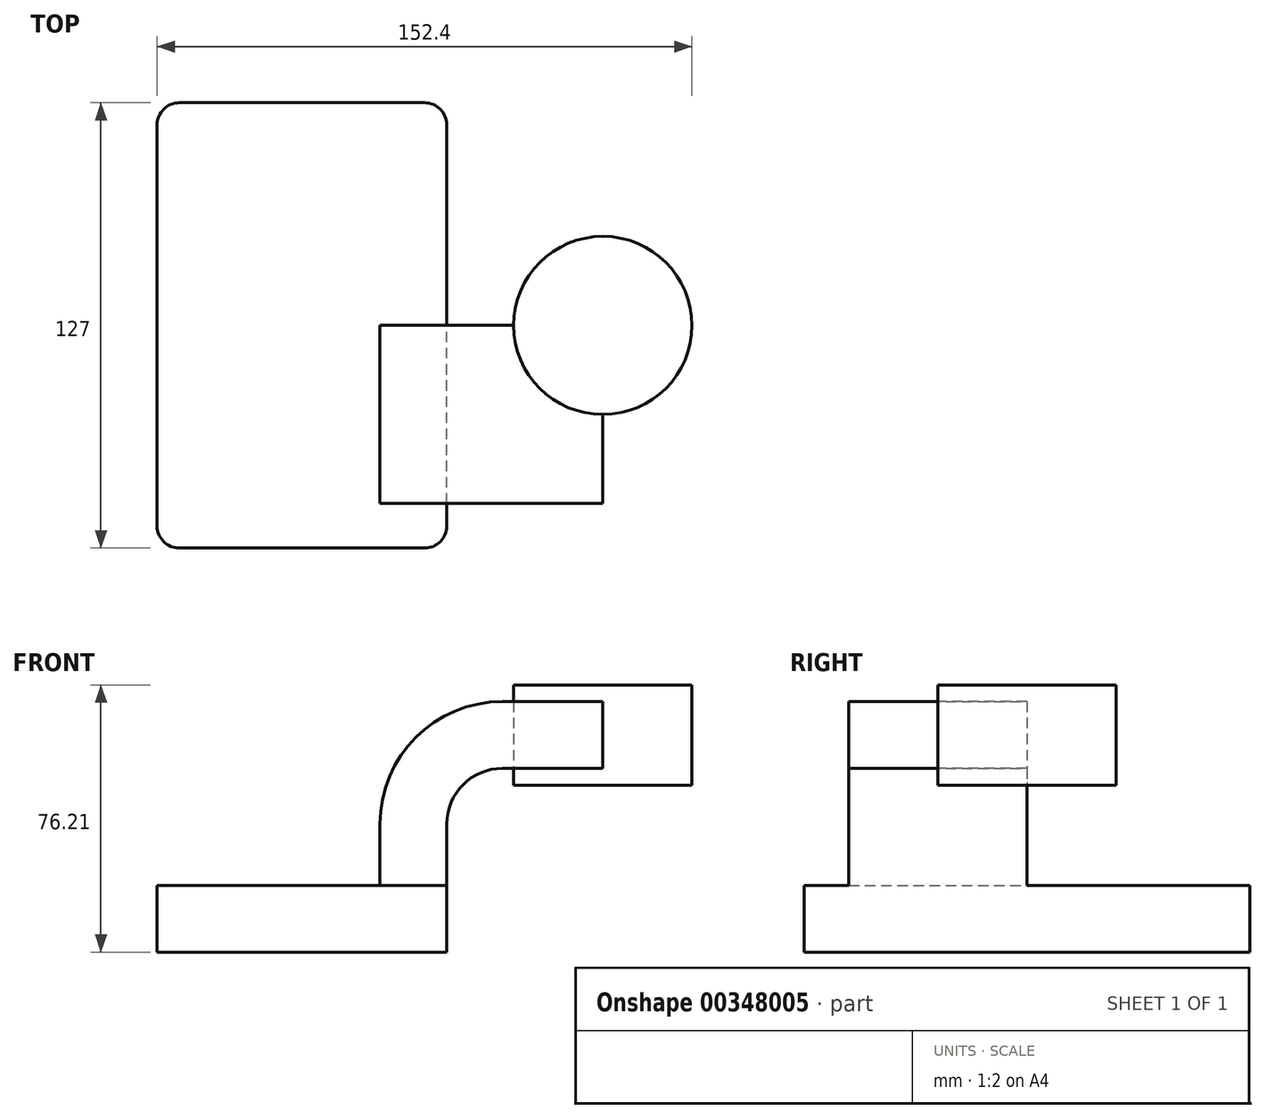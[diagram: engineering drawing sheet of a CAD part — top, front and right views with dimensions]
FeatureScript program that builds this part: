
annotation { "Feature Type Name" : "Feature", "Feature Type Description" : "" }
export const myFeature = defineFeature(function(context is Context, id is Id, definition is map)
    precondition{}
    {
        {
            var Q0;
            Q0=qCreatedBy(makeId("Front.planeOp"),FACE);
            var sketch = newSketch(context, id + "F0", { "sketchPlane" : qUnion([Q0])});
            skLineSegment(sketch, "E0.bottom", {"start": v(41.27, 9.53) * mm, "end": v(-41.28, 9.53) * mm});
            skLineSegment(sketch, "E0.top", {"start": v(41.28, -9.52) * mm, "end": v(-41.27, -9.52) * mm});
            skLineSegment(sketch, "E0.left", {"start": v(41.28, 9.53) * mm, "end": v(41.28, -9.52) * mm});
            skLineSegment(sketch, "E0.right", {"start": v(-41.28, 9.53) * mm, "end": v(-41.27, -9.52) * mm});
            skPoint(sketch, "E0.middle", {"position": v(0, 0) * mm});
            skLineSegment(sketch, "E1.bottom", {"start": v(111.12, 38.1) * mm, "end": v(60.32, 38.1) * mm});
            skLineSegment(sketch, "E1.top", {"start": v(111.12, 66.68) * mm, "end": v(60.32, 66.68) * mm});
            skLineSegment(sketch, "E1.left", {"start": v(111.12, 38.1) * mm, "end": v(111.12, 66.68) * mm});
            skLineSegment(sketch, "E1.right", {"start": v(60.32, 38.1) * mm, "end": v(60.32, 66.68) * mm});
            skPoint(sketch, "E1.middle", {"position": v(85.73, 52.39) * mm});
            skLineSegment(sketch, "E2", {"start": v(41.27, 9.53) * mm, "end": v(41.27, 27) * mm});
            skArc(sketch, "E3", {"start": v(41.28, 27) * mm, "mid": v(45.92, 38.23) * mm, "end": v(57.15, 42.88) * mm});
            skLineSegment(sketch, "E4", {"start": v(57.15, 42.88) * mm, "end": v(74.94, 42.88) * mm});
            skLineSegment(sketch, "E5", {"start": v(74.94, 42.88) * mm, "end": v(86.6, 42.88) * mm});
            skLineSegment(sketch, "E6", {"start": v(109.19, -23.17) * mm, "end": v(107.34, -21.62) * mm});
            skLineSegment(sketch, "E7.0", {"start": v(74.94, 61.93) * mm, "end": v(85.73, 61.93) * mm});
            skLineSegment(sketch, "E7.1", {"start": v(57.15, 61.93) * mm, "end": v(74.94, 61.93) * mm});
            skArc(sketch, "E7.2", {"start": v(22.23, 27) * mm, "mid": v(32.45, 51.7) * mm, "end": v(57.15, 61.93) * mm});
            skLineSegment(sketch, "E7.3", {"start": v(22.22, 9.53) * mm, "end": v(22.22, 27) * mm});
            skLineSegment(sketch, "E8", {"start": v(85.73, 38.1) * mm, "end": v(85.73, 66.68) * mm});
            skFitSpline(sketch, "E9", {"points": [v(-41.28, 9.53) * mm, v(57.15, 61.93) * mm], "startDerivative": vector(0.12, 127.1) * mm, "endDerivative": vector(139.48, -7.9) * mm});
            skSolve(sketch);
        }
        {
            var Q0;
            Q0=makeQuery(id+"F0.imprint","IMPRINT",FACE,{"disambiguationData":[TD([[makeQuery(id+"F0.imprint","IMPRINT",EDGE,{"derivedFrom":sQuery(id+"F0.wireOp",EDGE,"E0.top")}),-1.0]])]});
            extrude(context, id + "F1", {"entities" : qUnion([Q0]), "endBound" : BoundingType.SYMMETRIC, "depth" : 127 * mm});
        }
        {
            var Q0;
            {var subQ1=sQuery(id+"F0.wireOp",EDGE,"E2");Q0=makeQuery(id+"F0.imprint","IMPRINT",FACE,{"disambiguationData":[TD([[makeQuery(id+"F0.imprint","IMPRINT",EDGE,{"derivedFrom":subQ1}),1.0]])]});}
            var Q1;
            {var subQ0=sQuery(id+"F0.wireOp",EDGE,"E7.0");Q1=makeQuery(id+"F0.imprint","IMPRINT",FACE,{"disambiguationData":[TD([[makeQuery(id+"F0.imprint","IMPRINT",EDGE,{"derivedFrom":subQ0}),-1.0]])]});}
            extrude(context, id + "F2", {"entities" : qUnion([Q0, Q1]), "operationType" : NewBodyOperationType.ADD, "depth" : 50.8 * mm});
        }
        {
            var Q0;
            Q0=makeQuery(id+"F0.imprint","IMPRINT",FACE,{"disambiguationData":[TD([[makeQuery(id+"F0.imprint","IMPRINT",EDGE,{"derivedFrom":sQuery(id+"F0.wireOp",EDGE,"E7.2")}),1.0]])]});
            extrude(context, id + "F3", {"entities" : qUnion([Q0]), "operationType" : NewBodyOperationType.ADD, "depth" : 15.88 * mm});
        }
        {
            var Q0;
            {var subQ4=sQuery(id+"F0.wireOp",EDGE,"E1.left");Q0=makeQuery(id+"F0.imprint","IMPRINT",FACE,{"disambiguationData":[TD([[makeQuery(id+"F0.imprint","IMPRINT",EDGE,{"derivedFrom":subQ4}),1.0]])]});}
            var Q1;
            Q1=sQuery(id+"F0.wireOp",EDGE,"E8");
            revolve(context, id + "F4", {"operationType" : NewBodyOperationType.ADD, "entities" : qUnion([Q0]), "axis" : qUnion([Q1]), "revolveType" : RevolveType.FULL});
        }
        {
            var Q0;
            Q0=makeQuery(id+"F1.opExtrude","CAP_EDGE",EDGE,{"disambiguationData":[OSD([sQuery(id+"F0.wireOp",EDGE,"E0.right")])],"isStart":false});
            var Q1;
            Q1=makeQuery(id+"F1.opExtrude","CAP_EDGE",EDGE,{"disambiguationData":[OSD([sQuery(id+"F0.wireOp",EDGE,"E0.left")])],"isStart":false});
            var Q2;
            Q2=makeQuery(id+"F1.opExtrude","CAP_EDGE",EDGE,{"disambiguationData":[OSD([sQuery(id+"F0.wireOp",EDGE,"E0.left")])],"isStart":true});
            var Q3;
            Q3=makeQuery(id+"F1.opExtrude","CAP_EDGE",EDGE,{"disambiguationData":[OSD([sQuery(id+"F0.wireOp",EDGE,"E0.right")])],"isStart":true});
            fillet(context, id + "F5", {"entities" : qUnion([Q0, Q1, Q2, Q3]), "radius" : 6.35 * mm, "tangentPropagation" : true, "allowEdgeOverflow" : false});
        }
    });
